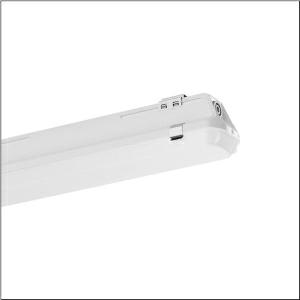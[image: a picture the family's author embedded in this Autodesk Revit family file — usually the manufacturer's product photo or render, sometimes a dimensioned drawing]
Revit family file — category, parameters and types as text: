
# Revit family: monsun_r__21_51fb107p430j_33ee
name_source: partatom
category: Lighting Fixtures
units: mm (PartAtom-declared; Revit-internal decimal feet)

## family parameters
Cut with Voids When Loaded = No
Host = Face
Light Source = No
Part Type = Normal
Room Calculation Point = No
Round Connector Dimension = Use Diameter
Shared = No

## types (1)
- Monsun® 21 (1 x LED, 3710 lm, 22.2 W, 4000K)
    Apparent Load = 22 VA
    CIE Flux Codes = 47 77 93 94 100
    Color Rendering = 80
    Color Temperature = 4000K
    Default Elevation = 1800 mm
    Description = Monsun® 21, damp-proof luminaire, chain hanger, primary optical cover: enclosure, of PMMA, light emission: direct distribution, primary light characteristic: symmetric, installation type: suspended mounting, surface-mounted, horizontal mounting, vertical mounting, LED, rated luminous flux: 3.710lm, luminous efficacy: 167lm/W, light colour: 840, colour temperature: 4000K, control gear: ECG, with terminal, 3-pole, max. 2.5mm², mains connection: 220..240V, AC, 50/60Hz, rated input power: 22W, housing, of glass-fibre reinforced polyester, uncoated, bright grey, incl. chain hanger, length: 1.590mm, width: 90mm, height: 88mm, clip for enclosure, of stainless steel (V2A), ceiling mounting element, of stainless steel (V2A), chain hanger, of stainless steel (V2A), protection rating (complete): IP66, insulation class (complete): insulation class I (protective earthing), certification: CE, ENEC, VDE, UKCA, protection symbol: D, impact resistance: IK04, permissible operating ambient temperature: -25..+35°C, standard: EN 50419, EN 60598-2-1, corresponds to IFS (International Featured Standards) requirements for safety and quality in the food industry, for indoor or canopied outdoor use, no direct snow, no direct sun, no direct rain, contact your sales advisor before using the luminaires in applications with unclear chemical exposure, large temperature fluctuations or condensation-forming humidity, LABS conformity tested according to VDMA 24364:2018-05, packaging unit: 1 piece
    Height = 89 mm
    Lamp = 1 x LED
    Lamp Light Flux = 3710 lm
    Lamp Power = 22.2 W
    Lamp count = 1
    Length = 1590 mm
    Luminous efficacy = 167 lm/W
    Manufacturer = Siteco
    ModVariant = No
    Model = 51FB107P430J
    Mounting Place = Ceiling
    Mounting Type = Surface mounted
    Number of Poles = 1
    OnlyDefault = Yes
    Power Factor = 1
    Product Name = Monsun® 21
    Product group = damp-proof luminaire
    ProductGroupID = 300
    Protection Class = Protection class I
    Protection Degree = IP 66
    RLX_Detail_Level = 1
    RLX_Emergency_Light_Flux = 0 lm
    RLX_Emergency_Type = 0
    RLX_Emergency_Type_DB = No
    RlxData = <blob elided: 88349 chars, md5=2a60ad86>
    Socket = socket
    Standby Power = 0 W
    System Light Flux = 3710 lm
    System Power = 22 W
    Type Comments = Product without accessories
    Type Image = l_1006717.jpg
    URL = http://relux.com
    VarID = ---
    Voltage = 0 V
    Weight = 0.00 kg
    Width = 90 mm

## geometry (parser evidence)
native form markers: Blend x4, Sweep x11
no freeform markers — native parametric forms only
